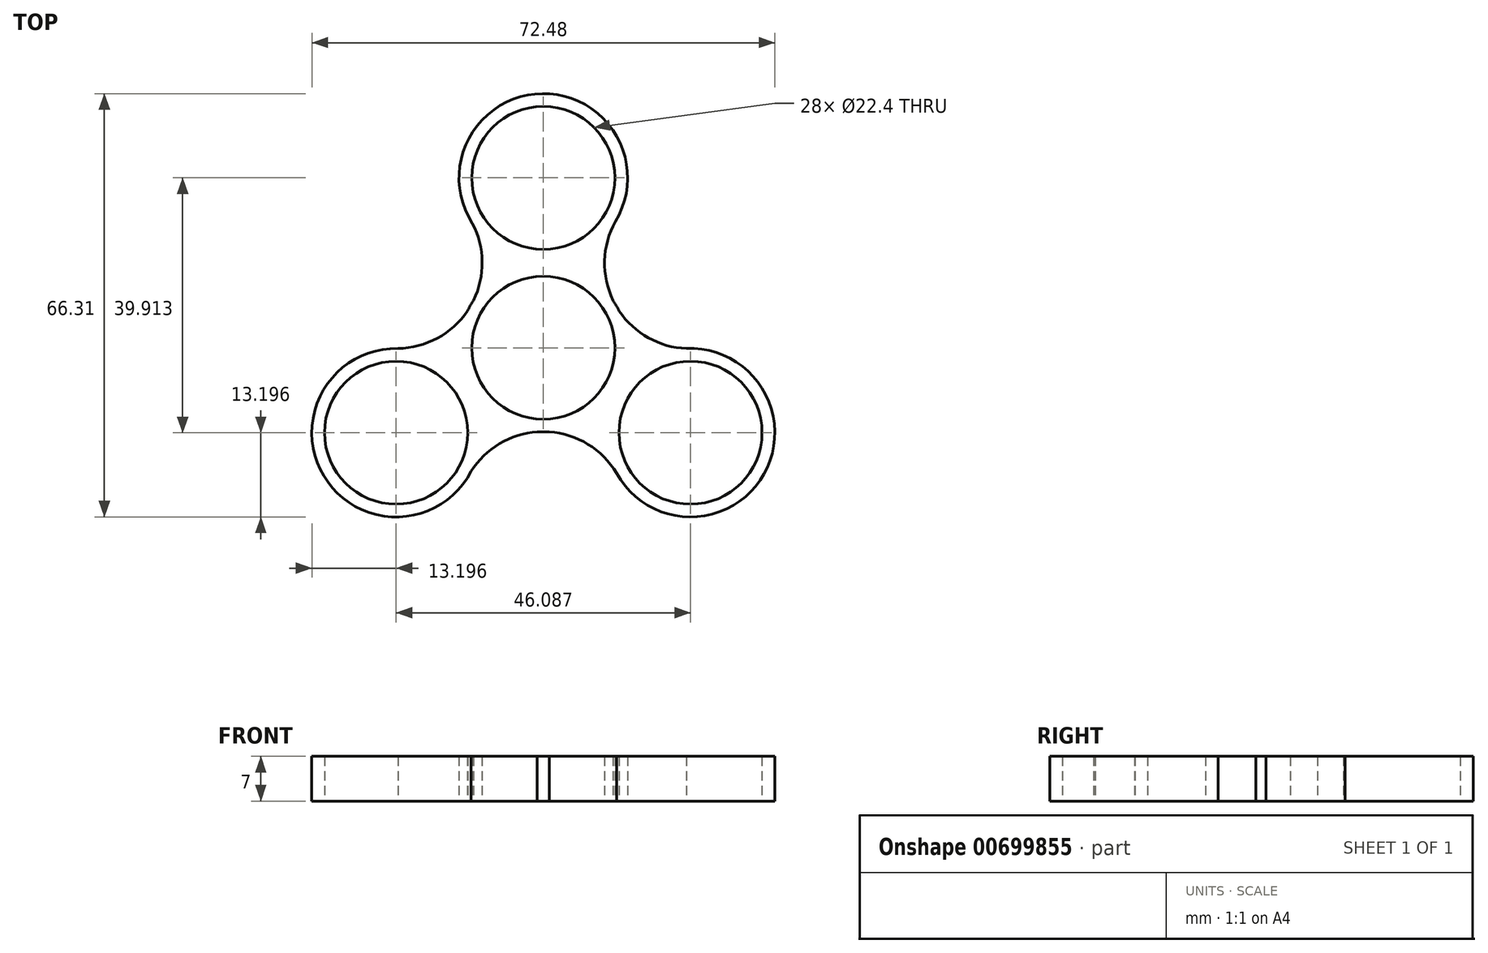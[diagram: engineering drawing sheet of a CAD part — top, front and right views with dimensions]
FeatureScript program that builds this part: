
annotation { "Feature Type Name" : "Feature", "Feature Type Description" : "" }
export const myFeature = defineFeature(function(context is Context, id is Id, definition is map)
    precondition{}
    {
        {
            var Q0;
            Q0=qCreatedBy(makeId("Top.planeOp"),FACE);
            var sketch = newSketch(context, id + "F0", { "sketchPlane" : qUnion([Q0])});
            skCircle(sketch, "E0", {"center": v(0, 0) * mm, "radius": 11.2 * mm});
            skArc(sketch, "E1", {"start": v(-10.93, 7.4) * mm, "mid": v(-11.43, 6.6) * mm, "end": v(-11.87, 5.77) * mm});
            skCircle(sketch, "E2", {"center": v(0, 26.6) * mm, "radius": 11.2 * mm});
            skArc(sketch, "E3", {"start": v(11.28, 19.76) * mm, "mid": v(-0.17, 39.8) * mm, "end": v(-11.1, 19.47) * mm});
            skArc(sketch, "E4.1.0", {"start": v(-22.75, -0.1) * mm, "mid": v(-34.39, -20.05) * mm, "end": v(-11.3, -19.35) * mm});
            skArc(sketch, "E4.2.0", {"start": v(11.47, -19.65) * mm, "mid": v(34.56, -19.76) * mm, "end": v(22.41, -0.12) * mm});
            skCircle(sketch, "E5.1.0", {"center": v(-23.04, -13.3) * mm, "radius": 11.2 * mm});
            skCircle(sketch, "E5.2.0", {"center": v(23.04, -13.3) * mm, "radius": 11.2 * mm});
            skArc(sketch, "E6", {"start": v(11.53, 20.18) * mm, "mid": v(11.17, 6.92) * mm, "end": v(22.41, -0.12) * mm});
            skArc(sketch, "E7.1.0", {"start": v(-23.24, -0.1) * mm, "mid": v(-11.58, 6.22) * mm, "end": v(-11.1, 19.47) * mm});
            skArc(sketch, "E7.2.0", {"start": v(11.71, -20.08) * mm, "mid": v(0.4, -13.14) * mm, "end": v(-11.3, -19.35) * mm});
            skArc(sketch, "E8.trimOffspring", {"start": v(-0.95, -13.17) * mm, "mid": v(0, -13.2) * mm, "end": v(0.94, -13.17) * mm});
            skArc(sketch, "E9.trimOffspring", {"start": v(11.88, 5.76) * mm, "mid": v(11.43, 6.6) * mm, "end": v(10.93, 7.4) * mm});
            skSolve(sketch);
        }
        {
            var Q0;
            Q0 = qSketchRegion(id + "F0", true);
            extrude(context, id + "F1", {"entities" : qUnion([Q0]), "depth" : 7 * mm, "offsetDistance" : 25 * mm});
        }
    });
